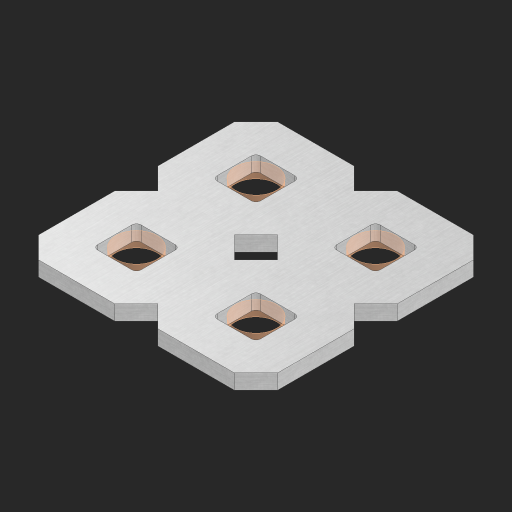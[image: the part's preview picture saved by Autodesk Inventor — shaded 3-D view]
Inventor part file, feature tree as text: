
AUTODESK INVENTOR PART (.ipt)
format: ipt  version: 2023 (Build 270158000, 158)  size: 342,016 bytes
history: native  units: in
note: dims shown in document units (in); Inventor stores cm internally (conversion verified against a paired STEP export)
features: other x5, extrude x3, sketch x2, pattern_linear x1
ambient origin geometry x8: Origin, YZ Plane, XZ Plane, XY Plane, X Axis, Y Axis, Z Axis, Center Point
bodies: Solid1 (feature_tree), Body (feature_tree)
feature tree (11):
  pattern_linear  "Rectangular Pattern1"  Spacing1=0.09in  [1 undecoded]
  sketch  "Sketch1"  dims[d1=0.5in]
  sketch  "Sketch2"  dims[d2=0.182in d3=0.09in d4=0.09in d5=0.09in d6=0.09in d7=0.09in d8=0.09in d9=0.09in d10=0.09in d11=0.02in d13=0.0in d14=0.172in d15=0.0625in d16=0.0in d19=0.5in d22=0.5in]
  other  "Srf1"
  other  "Srf126"
  other  "Srf268"
  other  "Srf269"
  other  "Circle"
  extrude  "ExtrusionSrf126"  Depth=0.09in
  extrude  "ExtrusionSrf268"  Depth=0.09in
  extrude  "ExtrusionSrf269"  Depth=0.09in
note: 1 required parameter value undecoded (feature->parameter linkage not recoverable at this tier; creation-order binding heuristic only, values carry confidence <= 0.55)
